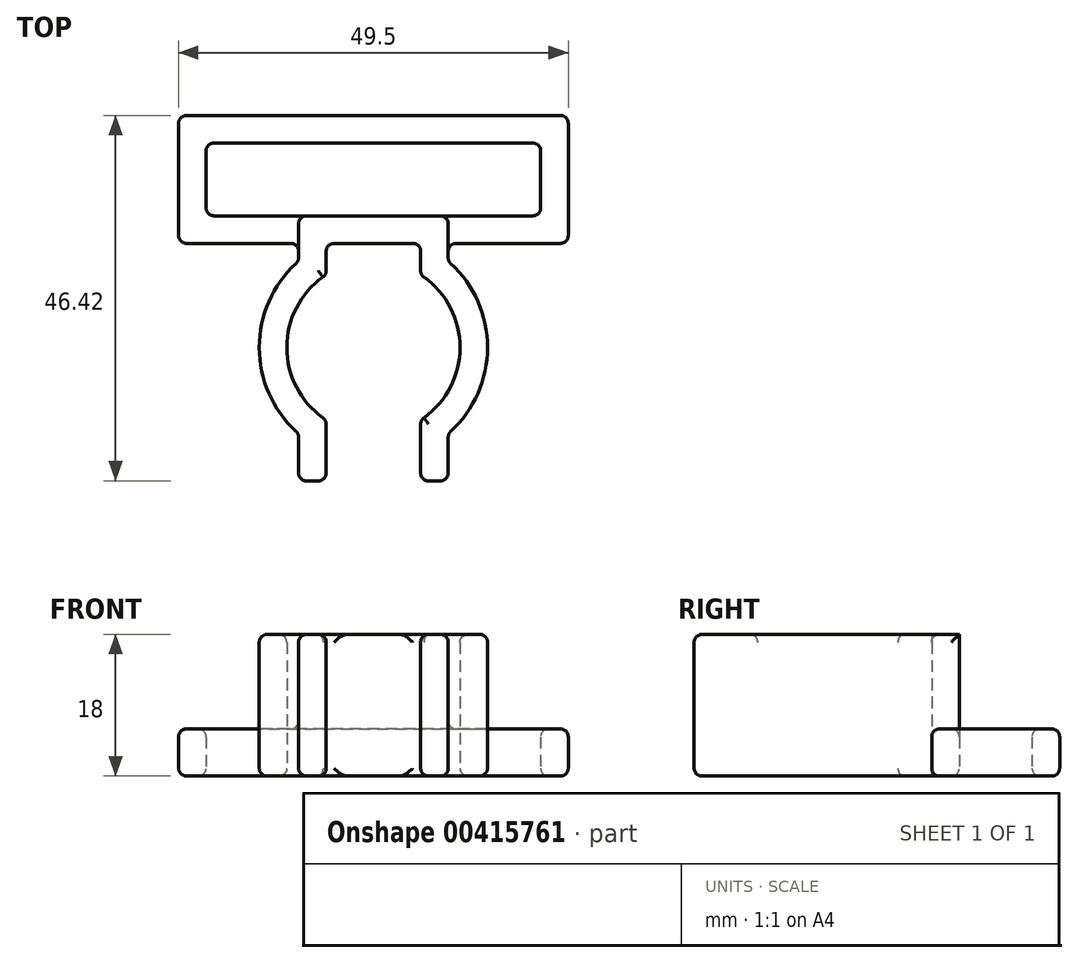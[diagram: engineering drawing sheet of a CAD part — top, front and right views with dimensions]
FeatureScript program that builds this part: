
annotation { "Feature Type Name" : "Feature", "Feature Type Description" : "" }
export const myFeature = defineFeature(function(context is Context, id is Id, definition is map)
    precondition{}
    {
        {
            var Q0;
            Q0=qCreatedBy(makeId("Top.planeOp"),FACE);
            var sketch = newSketch(context, id + "F0", { "sketchPlane" : qUnion([Q0])});
            skArc(sketch, "E0", {"start": v(-6, 9.22) * mm, "mid": v(-11, 0) * mm, "end": v(-6, -9.22) * mm});
            skArc(sketch, "E1", {"start": v(-9.5, 10.95) * mm, "mid": v(-14.5, 0) * mm, "end": v(-9.5, -10.95) * mm});
            skLineSegment(sketch, "E2", {"start": v(-9.5, -10.95) * mm, "end": v(-9.5, -16.95) * mm});
            skLineSegment(sketch, "E3", {"start": v(-9.5, -16.95) * mm, "end": v(-6, -16.95) * mm});
            skLineSegment(sketch, "E4", {"start": v(-6, -16.95) * mm, "end": v(-6, -9.22) * mm});
            skLineSegment(sketch, "E5", {"start": v(6, -9.22) * mm, "end": v(6, -16.95) * mm});
            skLineSegment(sketch, "E6", {"start": v(6, -16.95) * mm, "end": v(9.5, -16.95) * mm});
            skLineSegment(sketch, "E7", {"start": v(9.5, -16.95) * mm, "end": v(9.5, -10.95) * mm});
            skLineSegment(sketch, "E8", {"start": v(-6, -9.22) * mm, "end": v(-6, 9.22) * mm, "construction": true});
            skLineSegment(sketch, "E9", {"start": v(6, -9.22) * mm, "end": v(6, 9.22) * mm, "construction": true});
            skLineSegment(sketch, "E10", {"start": v(-6, 9.22) * mm, "end": v(-6, 13.22) * mm});
            skLineSegment(sketch, "E11", {"start": v(-6, 13.22) * mm, "end": v(6, 13.22) * mm});
            skLineSegment(sketch, "E12", {"start": v(6, 13.22) * mm, "end": v(6, 9.22) * mm});
            skArc(sketch, "E13.trimOffspring", {"start": v(6, -9.22) * mm, "mid": v(11, 0) * mm, "end": v(6, 9.22) * mm});
            skArc(sketch, "E14.trimOffspring", {"start": v(9.5, -10.95) * mm, "mid": v(14.5, 0) * mm, "end": v(9.5, 10.95) * mm});
            skLineSegment(sketch, "E15", {"start": v(-9.5, 10.95) * mm, "end": v(-9.5, 16.72) * mm});
            skLineSegment(sketch, "E16", {"start": v(-9.5, 16.72) * mm, "end": v(9.5, 16.72) * mm});
            skLineSegment(sketch, "E17", {"start": v(9.5, 16.72) * mm, "end": v(9.5, 10.95) * mm});
            skLineSegment(sketch, "E18.bottom", {"start": v(-21.25, 16.72) * mm, "end": v(21.25, 16.72) * mm});
            skLineSegment(sketch, "E18.top", {"start": v(-21.25, 25.97) * mm, "end": v(21.25, 25.97) * mm});
            skLineSegment(sketch, "E18.left", {"start": v(-21.25, 16.72) * mm, "end": v(-21.25, 25.97) * mm});
            skLineSegment(sketch, "E18.right", {"start": v(21.25, 16.72) * mm, "end": v(21.25, 25.97) * mm});
            skLineSegment(sketch, "E19.bottom", {"start": v(24.75, 13.22) * mm, "end": v(-24.75, 13.22) * mm});
            skLineSegment(sketch, "E19.top", {"start": v(24.75, 29.47) * mm, "end": v(-24.75, 29.47) * mm});
            skLineSegment(sketch, "E19.left", {"start": v(24.75, 13.22) * mm, "end": v(24.75, 29.47) * mm});
            skLineSegment(sketch, "E19.right", {"start": v(-24.75, 13.22) * mm, "end": v(-24.75, 29.47) * mm});
            skSolve(sketch);
        }
        {
            var Q0;
            Q0=makeQuery(id+"F0.imprint","IMPRINT",FACE,{"disambiguationData":[TD([[makeQuery(id+"F0.imprint","IMPRINT",EDGE,{"derivedFrom":sQuery(id+"F0.wireOp",EDGE,"E0")}),-1.0]])]});
            var Q1;
            Q1=makeQuery(id+"F0.imprint","IMPRINT",FACE,{"disambiguationData":[TD([[makeQuery(id+"F0.imprint","IMPRINT",EDGE,{"derivedFrom":sQuery(id+"F0.wireOp",EDGE,"E5")}),1.0]])]});
            var Q2;
            Q2=makeQuery(id+"F0.imprint","IMPRINT",FACE,{"disambiguationData":[TD([[makeQuery(id+"F0.imprint","IMPRINT",EDGE,{"derivedFrom":sQuery(id+"F0.wireOp",EDGE,"E18.top")}),1.0]])]});
            var Q3;
            {var subQ0=sQuery(id+"F0.wireOp",EDGE,"E18.bottom");var subQ1=sQuery(id+"F0.wireOp",EDGE,"E15");var subQ2=makeQuery(id+"F0.imprint","INTERSECT",VERTEX,{"derivedFrom":[subQ1,subQ0]});Q3=makeQuery(id+"F0.imprint","IMPRINT",FACE,{"disambiguationData":[TD([[makeQuery(id+"F0.imprint","IMPRINT",EDGE,{"disambiguationData":[TD([[subQ2,1.0]])],"derivedFrom":subQ1}),-1.0]])]});}
            extrude(context, id + "F1", {"entities" : qUnion([Q0, Q1, Q2, Q3]), "depth" : 6 * mm});
        }
        {
            var Q0;
            Q0=makeQuery(id+"F0.imprint","IMPRINT",FACE,{"disambiguationData":[TD([[makeQuery(id+"F0.imprint","IMPRINT",EDGE,{"derivedFrom":sQuery(id+"F0.wireOp",EDGE,"E5")}),1.0]])]});
            var Q1;
            Q1=makeQuery(id+"F0.imprint","IMPRINT",FACE,{"disambiguationData":[TD([[makeQuery(id+"F0.imprint","IMPRINT",EDGE,{"derivedFrom":sQuery(id+"F0.wireOp",EDGE,"E0")}),-1.0]])]});
            var Q2;
            {var subQ0=sQuery(id+"F0.wireOp",EDGE,"E18.bottom");var subQ1=sQuery(id+"F0.wireOp",EDGE,"E15");var subQ2=makeQuery(id+"F0.imprint","INTERSECT",VERTEX,{"derivedFrom":[subQ1,subQ0]});Q2=makeQuery(id+"F0.imprint","IMPRINT",FACE,{"disambiguationData":[TD([[makeQuery(id+"F0.imprint","IMPRINT",EDGE,{"disambiguationData":[TD([[subQ2,1.0]])],"derivedFrom":subQ1}),-1.0]])]});}
            extrude(context, id + "F2", {"entities" : qUnion([Q0, Q1, Q2]), "operationType" : NewBodyOperationType.ADD, "depth" : 18 * mm});
        }
        {
            var Q0;
            Q0=makeQuery(id+"F2.opExtrude","CAP_EDGE",EDGE,{"disambiguationData":[OSD([sQuery(id+"F0.wireOp",EDGE,"E12")])],"isStart":false});
            var Q1;
            {var subQ0=sQuery(id+"F0.wireOp",EDGE,"E19.bottom");Q1=makeQuery(id+"F1.opExtrude","CAP_EDGE",EDGE,{"disambiguationData":[OSD([subQ0]),TDD([makeQuery(id+"F0.imprint","IMPRINT",EDGE,{"disambiguationData":[TD([[makeQuery(id+"F0.imprint","INTERSECT",VERTEX,{"derivedFrom":[subQ0,sQuery(id+"F0.wireOp",EDGE,"E19.right")]}),1.0]])],"derivedFrom":subQ0})])],"isStart":false});}
            var Q2;
            {var subQ0=sQuery(id+"F0.wireOp",EDGE,"E7");var subQ1=sQuery(id+"F0.wireOp",EDGE,"E6");Q2=makeQuery(id+"F2.boolean.opBoolean","MERGE",EDGE,{"derivedFrom":[makeQuery(id+"F1.opExtrude","SWEPT_EDGE",EDGE,{"disambiguationData":[OSD([subQ1,subQ0])]}),makeQuery(id+"F2.opExtrude","SWEPT_EDGE",EDGE,{"disambiguationData":[OSD([subQ1,subQ0])]})]});}
            var Q3;
            Q3=makeQuery(id+"F2.opExtrude","CAP_EDGE",EDGE,{"disambiguationData":[OSD([sQuery(id+"F0.wireOp",EDGE,"E1")])],"isStart":false});
            var Q4;
            {var subQ0=sQuery(id+"F0.wireOp",EDGE,"E19.bottom");var subQ1=sQuery(id+"F0.wireOp",EDGE,"E12");Q4=makeQuery(id+"F2.boolean.opBoolean","MERGE",EDGE,{"derivedFrom":[makeQuery(id+"F1.opExtrude","SWEPT_EDGE",EDGE,{"disambiguationData":[OSD([subQ1,subQ0])]}),makeQuery(id+"F2.opExtrude","SWEPT_EDGE",EDGE,{"disambiguationData":[OSD([subQ1,subQ0])]})]});}
            var Q5;
            Q5=makeQuery(id+"F2.opExtrude","CAP_EDGE",EDGE,{"disambiguationData":[OSD([sQuery(id+"F0.wireOp",EDGE,"E4")])],"isStart":false});
            var Q6;
            {var subQ0=sQuery(id+"F0.wireOp",EDGE,"E19.bottom");Q6=makeQuery(id+"F1.opExtrude","CAP_EDGE",EDGE,{"disambiguationData":[OSD([subQ0]),TDD([makeQuery(id+"F0.imprint","IMPRINT",EDGE,{"disambiguationData":[TD([[makeQuery(id+"F0.imprint","INTERSECT",VERTEX,{"derivedFrom":[subQ0,sQuery(id+"F0.wireOp",EDGE,"E19.left")]}),-1.0]])],"derivedFrom":subQ0})])],"isStart":false});}
            var Q7;
            Q7=makeQuery(id+"F2.opExtrude","CAP_EDGE",EDGE,{"disambiguationData":[OSD([sQuery(id+"F0.wireOp",EDGE,"E0")])],"isStart":false});
            var Q8;
            Q8=makeQuery(id+"F1.opExtrude","CAP_EDGE",EDGE,{"disambiguationData":[OSD([sQuery(id+"F0.wireOp",EDGE,"E5")])],"isStart":true});
            var Q9;
            Q9=makeQuery(id+"F2.opExtrude","CAP_EDGE",EDGE,{"disambiguationData":[OSD([sQuery(id+"F0.wireOp",EDGE,"E15")])],"isStart":false});
            var Q10;
            {var subQ0=sQuery(id+"F0.wireOp",EDGE,"E4");var subQ1=sQuery(id+"F0.wireOp",EDGE,"E3");Q10=makeQuery(id+"F2.boolean.opBoolean","MERGE",EDGE,{"derivedFrom":[makeQuery(id+"F1.opExtrude","SWEPT_EDGE",EDGE,{"disambiguationData":[OSD([subQ1,subQ0])]}),makeQuery(id+"F2.opExtrude","SWEPT_EDGE",EDGE,{"disambiguationData":[OSD([subQ1,subQ0])]})]});}
            var Q11;
            {var subQ0=sQuery(id+"F0.wireOp",EDGE,"E3");var subQ1=sQuery(id+"F0.wireOp",EDGE,"E2");Q11=makeQuery(id+"F2.boolean.opBoolean","MERGE",EDGE,{"derivedFrom":[makeQuery(id+"F1.opExtrude","SWEPT_EDGE",EDGE,{"disambiguationData":[OSD([subQ1,subQ0])]}),makeQuery(id+"F2.opExtrude","SWEPT_EDGE",EDGE,{"disambiguationData":[OSD([subQ1,subQ0])]})]});}
            var Q12;
            Q12=makeQuery(id+"F1.opExtrude","SWEPT_EDGE",EDGE,{"disambiguationData":[OSD([sQuery(id+"F0.wireOp",EDGE,"E19.bottom"),sQuery(id+"F0.wireOp",EDGE,"E19.right")])]});
            var Q13;
            Q13=makeQuery(id+"F1.opExtrude","CAP_EDGE",EDGE,{"disambiguationData":[OSD([sQuery(id+"F0.wireOp",EDGE,"E19.top")])],"isStart":false});
            var Q14;
            Q14=makeQuery(id+"F2.opExtrude","CAP_EDGE",EDGE,{"disambiguationData":[OSD([sQuery(id+"F0.wireOp",EDGE,"E10")])],"isStart":false});
            var Q15;
            Q15=makeQuery(id+"F1.opExtrude","CAP_EDGE",EDGE,{"disambiguationData":[OSD([sQuery(id+"F0.wireOp",EDGE,"E19.left")])],"isStart":false});
            var Q16;
            {var subQ0=sQuery(id+"F0.wireOp",EDGE,"E6");var subQ1=sQuery(id+"F0.wireOp",EDGE,"E5");Q16=makeQuery(id+"F2.boolean.opBoolean","MERGE",EDGE,{"derivedFrom":[makeQuery(id+"F1.opExtrude","SWEPT_EDGE",EDGE,{"disambiguationData":[OSD([subQ1,subQ0])]}),makeQuery(id+"F2.opExtrude","SWEPT_EDGE",EDGE,{"disambiguationData":[OSD([subQ1,subQ0])]})]});}
            var Q17;
            Q17=makeQuery(id+"F1.opExtrude","CAP_EDGE",EDGE,{"disambiguationData":[OSD([sQuery(id+"F0.wireOp",EDGE,"E18.top")])],"isStart":true});
            var Q18;
            Q18=makeQuery(id+"F1.opExtrude","CAP_EDGE",EDGE,{"disambiguationData":[OSD([sQuery(id+"F0.wireOp",EDGE,"E19.right")])],"isStart":true});
            var Q19;
            Q19=makeQuery(id+"F2.opExtrude","CAP_EDGE",EDGE,{"disambiguationData":[OSD([sQuery(id+"F0.wireOp",EDGE,"E2")])],"isStart":false});
            var Q20;
            Q20=makeQuery(id+"F1.opExtrude","CAP_EDGE",EDGE,{"disambiguationData":[OSD([sQuery(id+"F0.wireOp",EDGE,"E18.top")])],"isStart":false});
            var Q21;
            Q21=makeQuery(id+"F1.opExtrude","CAP_EDGE",EDGE,{"disambiguationData":[OSD([sQuery(id+"F0.wireOp",EDGE,"E19.right")])],"isStart":false});
            var Q22;
            Q22=makeQuery(id+"F1.opExtrude","CAP_EDGE",EDGE,{"disambiguationData":[OSD([sQuery(id+"F0.wireOp",EDGE,"E0")])],"isStart":true});
            var Q23;
            Q23=makeQuery(id+"F2.opExtrude","CAP_EDGE",EDGE,{"disambiguationData":[OSD([sQuery(id+"F0.wireOp",EDGE,"E7")])],"isStart":false});
            var Q24;
            Q24=makeQuery(id+"F2.opExtrude","CAP_EDGE",EDGE,{"disambiguationData":[OSD([sQuery(id+"F0.wireOp",EDGE,"E13.trimOffspring")])],"isStart":false});
            var Q25;
            Q25=makeQuery(id+"F1.opExtrude","CAP_EDGE",EDGE,{"disambiguationData":[OSD([sQuery(id+"F0.wireOp",EDGE,"E18.left")])],"isStart":false});
            var Q26;
            Q26=makeQuery(id+"F1.opExtrude","CAP_EDGE",EDGE,{"disambiguationData":[OSD([sQuery(id+"F0.wireOp",EDGE,"E1")])],"isStart":true});
            var Q27;
            Q27=makeQuery(id+"F1.opExtrude","CAP_EDGE",EDGE,{"disambiguationData":[OSD([sQuery(id+"F0.wireOp",EDGE,"E12")])],"isStart":true});
            var Q28;
            Q28=makeQuery(id+"F1.opExtrude","CAP_EDGE",EDGE,{"disambiguationData":[OSD([sQuery(id+"F0.wireOp",EDGE,"E18.right")])],"isStart":true});
            var Q29;
            Q29=makeQuery(id+"F2.opExtrude","CAP_EDGE",EDGE,{"disambiguationData":[OSD([sQuery(id+"F0.wireOp",EDGE,"E14.trimOffspring")])],"isStart":false});
            var Q30;
            Q30=makeQuery(id+"F2.opExtrude","CAP_EDGE",EDGE,{"disambiguationData":[OSD([sQuery(id+"F0.wireOp",EDGE,"E3")])],"isStart":false});
            var Q31;
            Q31=makeQuery(id+"F1.opExtrude","CAP_EDGE",EDGE,{"disambiguationData":[OSD([sQuery(id+"F0.wireOp",EDGE,"E2")])],"isStart":true});
            var Q32;
            Q32=makeQuery(id+"F1.opExtrude","CAP_EDGE",EDGE,{"disambiguationData":[OSD([sQuery(id+"F0.wireOp",EDGE,"E13.trimOffspring")])],"isStart":true});
            var Q33;
            {var subQ0=sQuery(id+"F0.wireOp",EDGE,"E19.bottom");Q33=makeQuery(id+"F1.opExtrude","CAP_EDGE",EDGE,{"disambiguationData":[OSD([subQ0]),TDD([makeQuery(id+"F0.imprint","IMPRINT",EDGE,{"disambiguationData":[TD([[makeQuery(id+"F0.imprint","INTERSECT",VERTEX,{"derivedFrom":[subQ0,sQuery(id+"F0.wireOp",EDGE,"E19.left")]}),-1.0]])],"derivedFrom":subQ0})])],"isStart":true});}
            var Q34;
            Q34=makeQuery(id+"F2.opExtrude","CAP_EDGE",EDGE,{"disambiguationData":[OSD([sQuery(id+"F0.wireOp",EDGE,"E5")])],"isStart":false});
            var Q35;
            Q35=makeQuery(id+"F2.opExtrude","CAP_EDGE",EDGE,{"disambiguationData":[OSD([sQuery(id+"F0.wireOp",EDGE,"E17")])],"isStart":false});
            var Q36;
            {var subQ1=sQuery(id+"F0.wireOp",EDGE,"E17");var subQ2=sQuery(id+"F0.wireOp",EDGE,"E18.bottom");Q36=makeQuery(id+"F2.boolean.opBoolean","SPLIT",EDGE,{"disambiguationData":[TD([makeQuery(id+"F1.opExtrude","SWEPT_FACE",FACE,{"disambiguationData":[OSD([subQ1])]})])],"derivedFrom":makeQuery(id+"F1.opExtrude","CAP_EDGE",EDGE,{"disambiguationData":[OSD([subQ2])],"isStart":false})});}
            var Q37;
            {var subQ0=sQuery(id+"F0.wireOp",EDGE,"E19.bottom");var subQ1=sQuery(id+"F0.wireOp",EDGE,"E10");Q37=makeQuery(id+"F2.boolean.opBoolean","MERGE",EDGE,{"derivedFrom":[makeQuery(id+"F1.opExtrude","SWEPT_EDGE",EDGE,{"disambiguationData":[OSD([subQ1,subQ0])]}),makeQuery(id+"F2.opExtrude","SWEPT_EDGE",EDGE,{"disambiguationData":[OSD([subQ1,subQ0])]})]});}
            var Q38;
            {var subQ0=sQuery(id+"F0.wireOp",EDGE,"E14.trimOffspring");var subQ1=sQuery(id+"F0.wireOp",EDGE,"E7");Q38=makeQuery(id+"F2.boolean.opBoolean","MERGE",EDGE,{"derivedFrom":[makeQuery(id+"F1.opExtrude","SWEPT_EDGE",EDGE,{"disambiguationData":[OSD([subQ1,subQ0])]}),makeQuery(id+"F2.opExtrude","SWEPT_EDGE",EDGE,{"disambiguationData":[OSD([subQ1,subQ0])]})]});}
            var Q39;
            Q39=makeQuery(id+"F1.opExtrude","SWEPT_EDGE",EDGE,{"disambiguationData":[OSD([sQuery(id+"F0.wireOp",EDGE,"E18.top"),sQuery(id+"F0.wireOp",EDGE,"E18.right")])]});
            var Q40;
            Q40=makeQuery(id+"F1.opExtrude","SWEPT_EDGE",EDGE,{"disambiguationData":[OSD([sQuery(id+"F0.wireOp",EDGE,"E18.bottom"),sQuery(id+"F0.wireOp",EDGE,"E18.right")])]});
            var Q41;
            Q41=makeQuery(id+"F1.opExtrude","SWEPT_EDGE",EDGE,{"disambiguationData":[OSD([sQuery(id+"F0.wireOp",EDGE,"E18.bottom"),sQuery(id+"F0.wireOp",EDGE,"E18.left")])]});
            var Q42;
            Q42=makeQuery(id+"F1.opExtrude","CAP_EDGE",EDGE,{"disambiguationData":[OSD([sQuery(id+"F0.wireOp",EDGE,"E19.top")])],"isStart":true});
            var Q43;
            {var subQ0=sQuery(id+"F0.wireOp",EDGE,"E19.bottom");Q43=makeQuery(id+"F1.opExtrude","CAP_EDGE",EDGE,{"disambiguationData":[OSD([subQ0]),TDD([makeQuery(id+"F0.imprint","IMPRINT",EDGE,{"disambiguationData":[TD([[makeQuery(id+"F0.imprint","INTERSECT",VERTEX,{"derivedFrom":[subQ0,sQuery(id+"F0.wireOp",EDGE,"E19.right")]}),1.0]])],"derivedFrom":subQ0})])],"isStart":true});}
            var Q44;
            Q44=makeQuery(id+"F1.opExtrude","CAP_EDGE",EDGE,{"disambiguationData":[OSD([sQuery(id+"F0.wireOp",EDGE,"E4")])],"isStart":true});
            var Q45;
            Q45=makeQuery(id+"F1.opExtrude","SWEPT_EDGE",EDGE,{"disambiguationData":[OSD([sQuery(id+"F0.wireOp",EDGE,"E18.top"),sQuery(id+"F0.wireOp",EDGE,"E18.left")])]});
            var Q46;
            Q46=makeQuery(id+"F1.opExtrude","CAP_EDGE",EDGE,{"disambiguationData":[OSD([sQuery(id+"F0.wireOp",EDGE,"E14.trimOffspring")])],"isStart":true});
            var Q47;
            Q47=makeQuery(id+"F1.opExtrude","CAP_EDGE",EDGE,{"disambiguationData":[OSD([sQuery(id+"F0.wireOp",EDGE,"E3")])],"isStart":true});
            var Q48;
            {var subQ0=sQuery(id+"F0.wireOp",EDGE,"E19.bottom");Q48=makeQuery(id+"F1.opExtrude","CAP_EDGE",EDGE,{"disambiguationData":[OSD([subQ0]),TDD([makeQuery(id+"F0.imprint","IMPRINT",EDGE,{"disambiguationData":[TD([[makeQuery(id+"F0.imprint","INTERSECT",VERTEX,{"derivedFrom":[sQuery(id+"F0.wireOp",EDGE,"E10"),subQ0]}),1.0]])],"derivedFrom":subQ0})])],"isStart":true});}
            var Q49;
            Q49=makeQuery(id+"F1.opExtrude","SWEPT_EDGE",EDGE,{"disambiguationData":[OSD([sQuery(id+"F0.wireOp",EDGE,"E19.bottom"),sQuery(id+"F0.wireOp",EDGE,"E19.left")])]});
            var Q50;
            {var subQ0=sQuery(id+"F0.wireOp",EDGE,"E4");var subQ1=sQuery(id+"F0.wireOp",EDGE,"E0");Q50=makeQuery(id+"F2.boolean.opBoolean","MERGE",EDGE,{"derivedFrom":[makeQuery(id+"F1.opExtrude","SWEPT_EDGE",EDGE,{"disambiguationData":[OSD([subQ1,subQ0])]}),makeQuery(id+"F2.opExtrude","SWEPT_EDGE",EDGE,{"disambiguationData":[OSD([subQ1,subQ0])]})]});}
            var Q51;
            {var subQ0=sQuery(id+"F0.wireOp",EDGE,"E13.trimOffspring");var subQ1=sQuery(id+"F0.wireOp",EDGE,"E5");Q51=makeQuery(id+"F2.boolean.opBoolean","MERGE",EDGE,{"derivedFrom":[makeQuery(id+"F1.opExtrude","SWEPT_EDGE",EDGE,{"disambiguationData":[OSD([subQ1,subQ0])]}),makeQuery(id+"F2.opExtrude","SWEPT_EDGE",EDGE,{"disambiguationData":[OSD([subQ1,subQ0])]})]});}
            var Q52;
            Q52=makeQuery(id+"F2.opExtrude","CAP_EDGE",EDGE,{"disambiguationData":[OSD([sQuery(id+"F0.wireOp",EDGE,"E6")])],"isStart":false});
            var Q53;
            {var subQ0=sQuery(id+"F0.wireOp",EDGE,"E2");var subQ1=sQuery(id+"F0.wireOp",EDGE,"E1");Q53=makeQuery(id+"F2.boolean.opBoolean","MERGE",EDGE,{"derivedFrom":[makeQuery(id+"F1.opExtrude","SWEPT_EDGE",EDGE,{"disambiguationData":[OSD([subQ1,subQ0])]}),makeQuery(id+"F2.opExtrude","SWEPT_EDGE",EDGE,{"disambiguationData":[OSD([subQ1,subQ0])]})]});}
            var Q54;
            Q54=makeQuery(id+"F1.opExtrude","CAP_EDGE",EDGE,{"disambiguationData":[OSD([sQuery(id+"F0.wireOp",EDGE,"E18.bottom")])],"isStart":true});
            var Q55;
            {var subQ0=sQuery(id+"F0.wireOp",EDGE,"E15");var subQ1=sQuery(id+"F0.wireOp",EDGE,"E1");Q55=makeQuery(id+"F2.boolean.opBoolean","MERGE",EDGE,{"derivedFrom":[makeQuery(id+"F1.opExtrude","SWEPT_EDGE",EDGE,{"disambiguationData":[OSD([subQ1,subQ0])]}),makeQuery(id+"F2.opExtrude","SWEPT_EDGE",EDGE,{"disambiguationData":[OSD([subQ1,subQ0])]})]});}
            var Q56;
            {var subQ0=sQuery(id+"F0.wireOp",EDGE,"E17");var subQ1=sQuery(id+"F0.wireOp",EDGE,"E14.trimOffspring");Q56=makeQuery(id+"F2.boolean.opBoolean","MERGE",EDGE,{"derivedFrom":[makeQuery(id+"F1.opExtrude","SWEPT_EDGE",EDGE,{"disambiguationData":[OSD([subQ1,subQ0])]}),makeQuery(id+"F2.opExtrude","SWEPT_EDGE",EDGE,{"disambiguationData":[OSD([subQ1,subQ0])]})]});}
            var Q57;
            Q57=makeQuery(id+"F2.opExtrude","SWEPT_EDGE",EDGE,{"disambiguationData":[OSD([sQuery(id+"F0.wireOp",EDGE,"E15"),sQuery(id+"F0.wireOp",EDGE,"E18.bottom")])]});
            var Q58;
            {var subQ0=sQuery(id+"F0.wireOp",EDGE,"E13.trimOffspring");var subQ1=sQuery(id+"F0.wireOp",EDGE,"E12");Q58=makeQuery(id+"F2.boolean.opBoolean","MERGE",EDGE,{"derivedFrom":[makeQuery(id+"F1.opExtrude","SWEPT_EDGE",EDGE,{"disambiguationData":[OSD([subQ1,subQ0])]}),makeQuery(id+"F2.opExtrude","SWEPT_EDGE",EDGE,{"disambiguationData":[OSD([subQ1,subQ0])]})]});}
            var Q59;
            Q59=makeQuery(id+"F1.opExtrude","SWEPT_EDGE",EDGE,{"disambiguationData":[OSD([sQuery(id+"F0.wireOp",EDGE,"E19.top"),sQuery(id+"F0.wireOp",EDGE,"E19.left")])]});
            var Q60;
            Q60=makeQuery(id+"F1.opExtrude","CAP_EDGE",EDGE,{"disambiguationData":[OSD([sQuery(id+"F0.wireOp",EDGE,"E6")])],"isStart":true});
            var Q61;
            Q61=makeQuery(id+"F1.opExtrude","CAP_EDGE",EDGE,{"disambiguationData":[OSD([sQuery(id+"F0.wireOp",EDGE,"E19.left")])],"isStart":true});
            var Q62;
            Q62=makeQuery(id+"F2.opExtrude","CAP_EDGE",EDGE,{"disambiguationData":[OSD([sQuery(id+"F0.wireOp",EDGE,"E18.bottom")])],"isStart":false});
            var Q63;
            Q63=makeQuery(id+"F1.opExtrude","SWEPT_EDGE",EDGE,{"disambiguationData":[OSD([sQuery(id+"F0.wireOp",EDGE,"E19.top"),sQuery(id+"F0.wireOp",EDGE,"E19.right")])]});
            var Q64;
            {var subQ0=sQuery(id+"F0.wireOp",EDGE,"E10");var subQ1=sQuery(id+"F0.wireOp",EDGE,"E0");Q64=makeQuery(id+"F2.boolean.opBoolean","MERGE",EDGE,{"derivedFrom":[makeQuery(id+"F1.opExtrude","SWEPT_EDGE",EDGE,{"disambiguationData":[OSD([subQ1,subQ0])]}),makeQuery(id+"F2.opExtrude","SWEPT_EDGE",EDGE,{"disambiguationData":[OSD([subQ1,subQ0])]})]});}
            var Q65;
            Q65=makeQuery(id+"F1.opExtrude","SWEPT_EDGE",EDGE,{"disambiguationData":[OSD([sQuery(id+"F0.wireOp",EDGE,"E15"),sQuery(id+"F0.wireOp",EDGE,"E19.bottom")])]});
            var Q66;
            Q66=makeQuery(id+"F1.opExtrude","CAP_EDGE",EDGE,{"disambiguationData":[OSD([sQuery(id+"F0.wireOp",EDGE,"E7")])],"isStart":true});
            var Q67;
            Q67=makeQuery(id+"F1.opExtrude","CAP_EDGE",EDGE,{"disambiguationData":[OSD([sQuery(id+"F0.wireOp",EDGE,"E10")])],"isStart":true});
            var Q68;
            Q68=makeQuery(id+"F1.opExtrude","CAP_EDGE",EDGE,{"disambiguationData":[OSD([sQuery(id+"F0.wireOp",EDGE,"E18.left")])],"isStart":true});
            var Q69;
            Q69=makeQuery(id+"F2.opExtrude","CAP_EDGE",EDGE,{"disambiguationData":[OSD([sQuery(id+"F0.wireOp",EDGE,"E19.bottom")])],"isStart":false});
            var Q70;
            Q70=makeQuery(id+"F1.opExtrude","CAP_EDGE",EDGE,{"disambiguationData":[OSD([sQuery(id+"F0.wireOp",EDGE,"E18.right")])],"isStart":false});
            var Q71;
            {var subQ0=sQuery(id+"F0.wireOp",EDGE,"E15");Q71=makeQuery(id+"F2.boolean.opBoolean","INTERSECT",EDGE,{"derivedFrom":[makeQuery(id+"F1.opExtrude","CAP_FACE",FACE,{"disambiguationData":[OSD([sQuery(id+"F0.wireOp",EDGE,"E0"),sQuery(id+"F0.wireOp",EDGE,"E1"),sQuery(id+"F0.wireOp",EDGE,"E2"),sQuery(id+"F0.wireOp",EDGE,"E3"),sQuery(id+"F0.wireOp",EDGE,"E4"),sQuery(id+"F0.wireOp",EDGE,"E5"),sQuery(id+"F0.wireOp",EDGE,"E6"),sQuery(id+"F0.wireOp",EDGE,"E7"),sQuery(id+"F0.wireOp",EDGE,"E10"),sQuery(id+"F0.wireOp",EDGE,"E12"),sQuery(id+"F0.wireOp",EDGE,"E13.trimOffspring"),sQuery(id+"F0.wireOp",EDGE,"E14.trimOffspring"),subQ0,sQuery(id+"F0.wireOp",EDGE,"E17"),sQuery(id+"F0.wireOp",EDGE,"E18.bottom"),sQuery(id+"F0.wireOp",EDGE,"E18.top"),sQuery(id+"F0.wireOp",EDGE,"E18.left"),sQuery(id+"F0.wireOp",EDGE,"E18.right"),sQuery(id+"F0.wireOp",EDGE,"E19.bottom"),sQuery(id+"F0.wireOp",EDGE,"E19.top"),sQuery(id+"F0.wireOp",EDGE,"E19.left"),sQuery(id+"F0.wireOp",EDGE,"E19.right")])],"isStart":false}),makeQuery(id+"F2.opExtrude","SWEPT_FACE",FACE,{"disambiguationData":[OSD([subQ0])]})]});}
            var Q72;
            {var subQ0=sQuery(id+"F0.wireOp",EDGE,"E17");Q72=makeQuery(id+"F2.boolean.opBoolean","INTERSECT",EDGE,{"derivedFrom":[makeQuery(id+"F1.opExtrude","CAP_FACE",FACE,{"disambiguationData":[OSD([sQuery(id+"F0.wireOp",EDGE,"E0"),sQuery(id+"F0.wireOp",EDGE,"E1"),sQuery(id+"F0.wireOp",EDGE,"E2"),sQuery(id+"F0.wireOp",EDGE,"E3"),sQuery(id+"F0.wireOp",EDGE,"E4"),sQuery(id+"F0.wireOp",EDGE,"E5"),sQuery(id+"F0.wireOp",EDGE,"E6"),sQuery(id+"F0.wireOp",EDGE,"E7"),sQuery(id+"F0.wireOp",EDGE,"E10"),sQuery(id+"F0.wireOp",EDGE,"E12"),sQuery(id+"F0.wireOp",EDGE,"E13.trimOffspring"),sQuery(id+"F0.wireOp",EDGE,"E14.trimOffspring"),sQuery(id+"F0.wireOp",EDGE,"E15"),subQ0,sQuery(id+"F0.wireOp",EDGE,"E18.bottom"),sQuery(id+"F0.wireOp",EDGE,"E18.top"),sQuery(id+"F0.wireOp",EDGE,"E18.left"),sQuery(id+"F0.wireOp",EDGE,"E18.right"),sQuery(id+"F0.wireOp",EDGE,"E19.bottom"),sQuery(id+"F0.wireOp",EDGE,"E19.top"),sQuery(id+"F0.wireOp",EDGE,"E19.left"),sQuery(id+"F0.wireOp",EDGE,"E19.right")])],"isStart":false}),makeQuery(id+"F2.opExtrude","SWEPT_FACE",FACE,{"disambiguationData":[OSD([subQ0])]})]});}
            var Q73;
            {var subQ1=sQuery(id+"F0.wireOp",EDGE,"E15");var subQ2=sQuery(id+"F0.wireOp",EDGE,"E18.bottom");Q73=makeQuery(id+"F2.boolean.opBoolean","SPLIT",EDGE,{"disambiguationData":[TD([makeQuery(id+"F1.opExtrude","SWEPT_FACE",FACE,{"disambiguationData":[OSD([subQ1])]})])],"derivedFrom":makeQuery(id+"F1.opExtrude","CAP_EDGE",EDGE,{"disambiguationData":[OSD([subQ2])],"isStart":false})});}
            var Q74;
            Q74=makeQuery(id+"F1.opExtrude","CAP_EDGE",EDGE,{"disambiguationData":[OSD([sQuery(id+"F0.wireOp",EDGE,"E17")])],"isStart":true});
            var Q75;
            Q75=makeQuery(id+"F1.opExtrude","CAP_EDGE",EDGE,{"disambiguationData":[OSD([sQuery(id+"F0.wireOp",EDGE,"E15")])],"isStart":true});
            var Q76;
            Q76=makeQuery(id+"F1.opExtrude","SWEPT_EDGE",EDGE,{"disambiguationData":[OSD([sQuery(id+"F0.wireOp",EDGE,"E17"),sQuery(id+"F0.wireOp",EDGE,"E19.bottom")])]});
            var Q77;
            Q77=makeQuery(id+"F2.opExtrude","SWEPT_EDGE",EDGE,{"disambiguationData":[OSD([sQuery(id+"F0.wireOp",EDGE,"E17"),sQuery(id+"F0.wireOp",EDGE,"E18.bottom")])]});
            fillet(context, id + "F3", {"entities" : qUnion([Q0, Q1, Q2, Q3, Q4, Q5, Q6, Q7, Q8, Q9, Q10, Q11, Q12, Q13, Q14, Q15, Q16, Q17, Q18, Q19, Q20, Q21, Q22, Q23, Q24, Q25, Q26, Q27, Q28, Q29, Q30, Q31, Q32, Q33, Q34, Q35, Q36, Q37, Q38, Q39, Q40, Q41, Q42, Q43, Q44, Q45, Q46, Q47, Q48, Q49, Q50, Q51, Q52, Q53, Q54, Q55, Q56, Q57, Q58, Q59, Q60, Q61, Q62, Q63, Q64, Q65, Q66, Q67, Q68, Q69, Q70, Q71, Q72, Q73, Q74, Q75, Q76, Q77]), "radius" : 1 * mm, "tangentPropagation" : true, "allowEdgeOverflow" : false});
        }
    });
